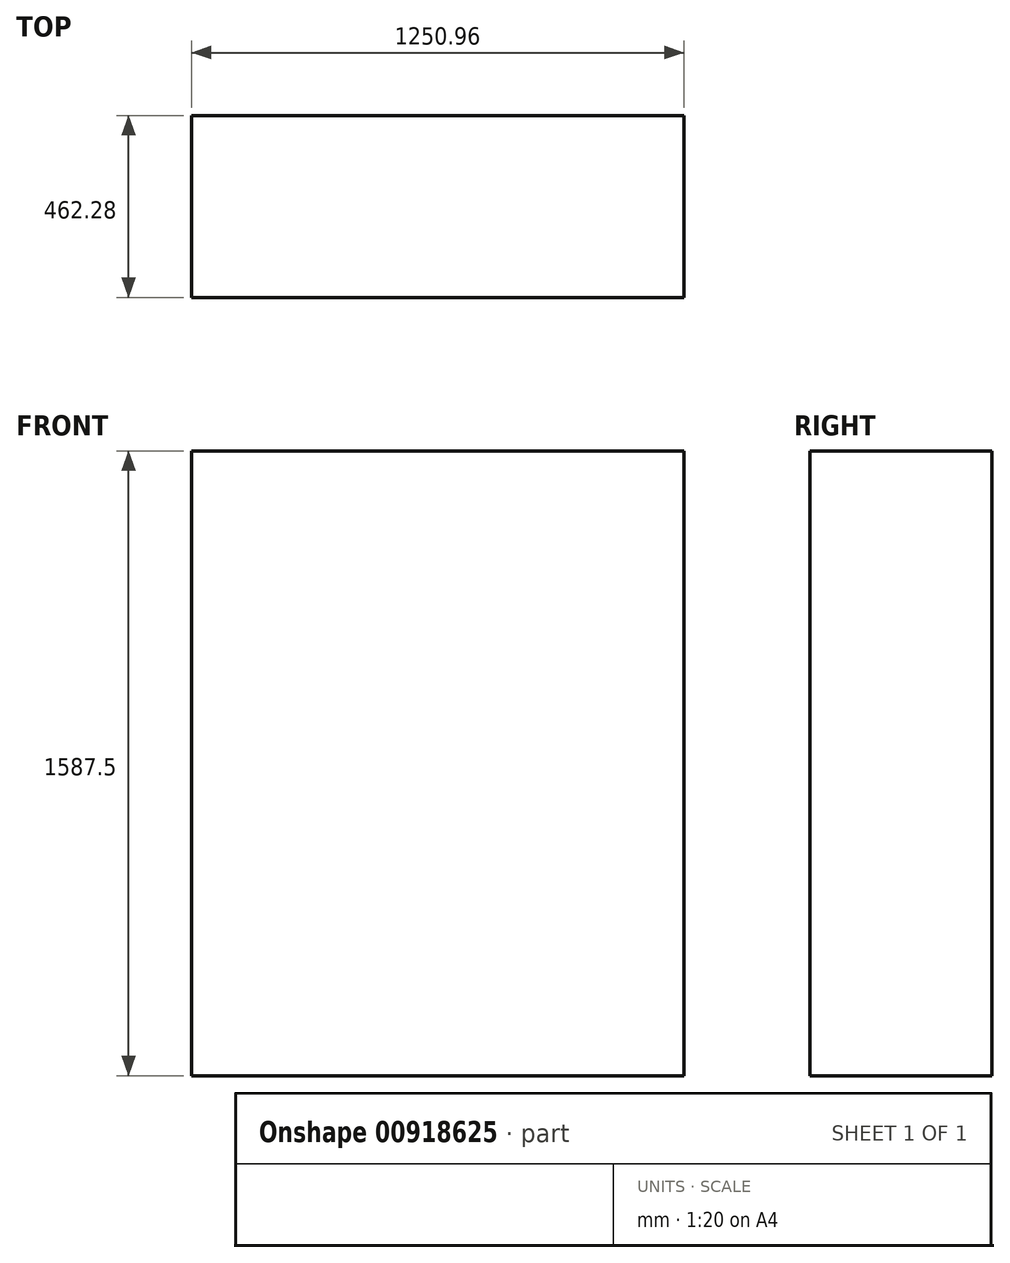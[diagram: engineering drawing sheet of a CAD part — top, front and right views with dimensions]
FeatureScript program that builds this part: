
annotation { "Feature Type Name" : "Feature", "Feature Type Description" : "" }
export const myFeature = defineFeature(function(context is Context, id is Id, definition is map)
    precondition{}
    {
        {
            var Q0;
            Q0=qCreatedBy(makeId("Front.planeOp"),FACE);
            var sketch = newSketch(context, id + "F0", { "sketchPlane" : qUnion([Q0])});
            skLineSegment(sketch, "E0.bottom", {"start": v(-625.48, 793.75) * mm, "end": v(625.48, 793.75) * mm});
            skLineSegment(sketch, "E0.top", {"start": v(-625.48, -793.75) * mm, "end": v(625.47, -793.75) * mm});
            skLineSegment(sketch, "E0.left", {"start": v(-625.48, 793.75) * mm, "end": v(-625.48, -793.75) * mm});
            skLineSegment(sketch, "E0.right", {"start": v(625.48, 793.75) * mm, "end": v(625.47, -793.75) * mm});
            skLineSegment(sketch, "E1", {"start": v(-625.48, 793.75) * mm, "end": v(625.47, -793.75) * mm, "construction": true});
            skSolve(sketch);
        }
        {
            var Q0;
            Q0=makeQuery(id+"F0.imprint","IMPRINT",FACE,{"disambiguationData":[TD([[makeQuery(id+"F0.imprint","IMPRINT",EDGE,{"derivedFrom":sQuery(id+"F0.wireOp",EDGE,"E0.bottom")}),-1.0]])]});
            extrude(context, id + "F1", {"entities" : qUnion([Q0]), "depth" : 462.28 * mm, "offsetDistance" : 25.4 * mm});
        }
    });
